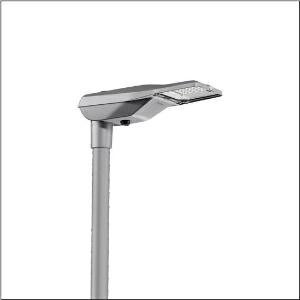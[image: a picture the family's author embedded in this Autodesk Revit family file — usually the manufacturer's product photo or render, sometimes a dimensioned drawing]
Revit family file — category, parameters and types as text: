
# Revit family: streetlight_sl_21_iq_micro___st1_0ab_5xe1m31u08db_013b
name_source: partatom
category: Lighting Fixtures
units: mm (PartAtom-declared; Revit-internal decimal feet)

## family parameters
Cut with Voids When Loaded = No
Host = Face
Light Source = No
Part Type = Normal
Room Calculation Point = No
Round Connector Dimension = Use Diameter
Shared = No

## types (1)
- --- (1 x LED, 4490 lm, 39.1 W, 3000K)
    Apparent Load = 39 VA
    CIE Flux Codes = 38 73 97 100 100
    Color Rendering = 70
    Color Temperature = 3000K
    Default Elevation = 1800 mm
    Description = Streetlight SL 21 iQ micro, mast luminaire, primary light control with lens, of PMMA, primary optical cover: cover, of toughened safety glass, transparent, light distribution: ST1.0aB, light emission: direct distribution, primary light characteristic: asymmetric, installation type: post-top, side-entry, LED, High Power LED, rated luminous flux: 4.490lm, luminous efficacy: 115lm/W, light colour: 730, colour temperature: 3000K, control: pre-setting: logarithmic dimming characteristic, Street-Remote, Auto-Match, Temp-Guard, Lumen-Switch, Night-Set, Smart-Wire, Light-Fading, Desk-Remote (wireless, voltage-free reading and setting of iQ features in the workshop via application-optimized NFC function/RFID function), optimised constant luminous flux control (CLO 2.0), mains connection: 220..240V, AC, 50/60Hz, start of lifetime: 39W, end of service life: 41W, reduction: 17W, luminaire housing, of diecast aluminium, powder-coated, Siteco® metallic grey (DB 702S), corrosivity category C5 mid according to DIN EN ISO 12944, please order mast flange separately, inclination adjustable: 0°, 5°, 10°, 15°, sealing non-destructively replaceable, multi-level sealing system, length: 528mm, width: 235mm, height: 110mm, mast flange for spigot size: 42mm (side-entry): 5XC10008XM4, 60/48mm (side-entry/post-top): 5XC10108XM2, 76/60mm (side-entry/post-top): 5XC10108XM1, Smart Interface below, protection rating (complete): IP66, insulation class (complete): insulation class II (safety insulation), certification: CE, ENEC, ENEC+, VDE, impact resistance: IK09, permissible operating ambient temperature for outdoor applications: -40..+50°C, standard-compliant lighting for roads and squares, packaging unit: 1 piece

Light Distribution: ST1.0aB
    Height = 110 mm
    Lamp = 1 x LED
    Lamp Light Flux = 4490 lm
    Lamp Power = 39.1 W
    Lamp count = 1
    Length = 528 mm
    Luminous efficacy = 115 lm/W
    Manufacturer = Siteco
    ModVariant = No
    Model = 5XE1M31U08DB
    Number of Poles = 1
    OnlyDefault = Yes
    Power Factor = 1
    Product Name = Streetlight SL 21 iQ micro | ST1.0aB
    Product group = mast luminaire | pylon top
    ProductGroupID = 6100
    Protection Class = Protection class II
    Protection Degree = IP 66
    RLX_Detail_Level = 1
    RLX_Emergency_Light_Flux = 0 lm
    RLX_Emergency_Type = 0
    RLX_Emergency_Type_DB = No
    RlxData = <blob elided: 98633 chars, md5=98932b26>
    Socket = socket
    Standby Power = 0 W
    System Light Flux = 4490 lm
    System Power = 39 W
    Type Comments = factory setting: luminous flux: 100 % | dim-lin: 254 | 765 mA
    Type Image = l_1277290.jpg
    URL = http://relux.com
    VarID = @adj_081633
    Voltage = 0 V
    Weight = 0.00 kg
    Width = 235 mm

## geometry (parser evidence)
native form markers: Blend x4, Sweep x11
no freeform markers — native parametric forms only
